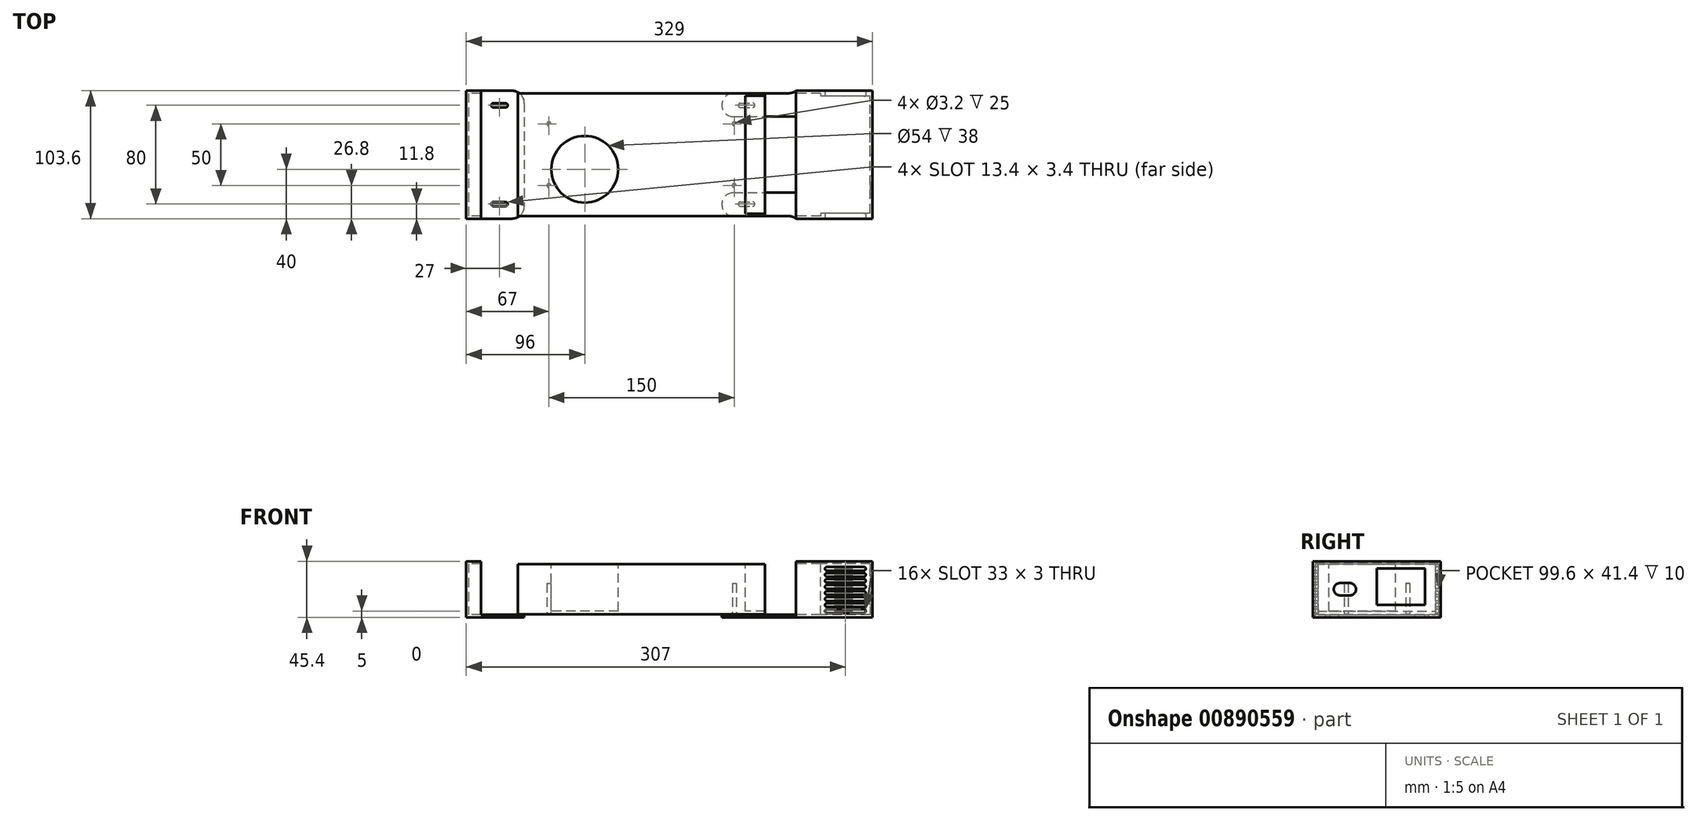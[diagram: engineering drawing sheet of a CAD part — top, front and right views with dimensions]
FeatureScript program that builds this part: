
annotation { "Feature Type Name" : "Feature", "Feature Type Description" : "" }
export const myFeature = defineFeature(function(context is Context, id is Id, definition is map)
    precondition{}
    {
        {
            var Q0;
            Q0=qCreatedBy(makeId("Top.planeOp"),FACE);
            var sketch = newSketch(context, id + "F0", { "sketchPlane" : qUnion([Q0])});
            skLineSegment(sketch, "E0.bottom", {"start": v(100, -49.8) * mm, "end": v(-100, -49.8) * mm});
            skLineSegment(sketch, "E0.top", {"start": v(100, 49.8) * mm, "end": v(-100, 49.8) * mm});
            skLineSegment(sketch, "E0.left", {"start": v(100, -49.8) * mm, "end": v(100, 49.8) * mm});
            skLineSegment(sketch, "E0.right", {"start": v(-100, -49.8) * mm, "end": v(-100, 49.8) * mm});
            skPoint(sketch, "E0.middle", {"position": v(0, 0) * mm});
            skSolve(sketch);
        }
        {
            var Q0;
            Q0=qSketchRegion(id+"F0",true);
            extrude(context, id + "F1", {"entities" : qUnion([Q0]), "depth" : 40.6 * mm, "offsetDistance" : 25 * mm});
        }
        {
            var Q0;
            Q0=makeQuery(id+"F1.opExtrude","CAP_FACE",FACE,{"disambiguationData":[OSD([sQuery(id+"F0.wireOp",EDGE,"E0.bottom"),sQuery(id+"F0.wireOp",EDGE,"E0.top"),sQuery(id+"F0.wireOp",EDGE,"E0.left"),sQuery(id+"F0.wireOp",EDGE,"E0.right")])],"isStart":false});
            var sketch = newSketch(context, id + "F2", { "sketchPlane" : qUnion([Q0])});
            skLineSegment(sketch, "E1.bottom", {"start": v(100, 47.8) * mm, "end": v(84, 47.8) * mm});
            skLineSegment(sketch, "E1.top", {"start": v(100, -47.8) * mm, "end": v(84, -47.8) * mm});
            skLineSegment(sketch, "E1.left", {"start": v(100, 47.8) * mm, "end": v(100, -47.8) * mm});
            skLineSegment(sketch, "E1.right", {"start": v(84, 47.8) * mm, "end": v(84, -47.8) * mm});
            skCircle(sketch, "E2", {"center": v(-46, -11.8) * mm, "radius": 27 * mm});
            skSolve(sketch);
        }
        {
            var Q0;
            Q0=qSketchRegion(id+"F2",true);
            extrude(context, id + "F3", {"entities" : qUnion([Q0]), "operationType" : NewBodyOperationType.REMOVE, "oppositeDirection" : true, "depth" : 38 * mm, "offsetDistance" : 25 * mm});
        }
        {
            var Q0;
            Q0=makeQuery(id+"F1.opExtrude","CAP_FACE",FACE,{"disambiguationData":[OSD([sQuery(id+"F0.wireOp",EDGE,"E0.bottom"),sQuery(id+"F0.wireOp",EDGE,"E0.top"),sQuery(id+"F0.wireOp",EDGE,"E0.left"),sQuery(id+"F0.wireOp",EDGE,"E0.right")])],"isStart":true});
            var sketch = newSketch(context, id + "F4", { "sketchPlane" : qUnion([Q0])});
            skCircle(sketch, "E3", {"center": v(-75, 25) * mm, "radius": 1.6 * mm});
            skCircle(sketch, "E4.MirrorC", {"center": v(75, 25) * mm, "radius": 1.6 * mm});
            skCircle(sketch, "E5.MirrorC", {"center": v(-75, -25) * mm, "radius": 1.6 * mm});
            skCircle(sketch, "E6.MirrorC", {"center": v(75, -25) * mm, "radius": 1.6 * mm});
            skSolve(sketch);
        }
        {
            var Q0;
            Q0=qSketchRegion(id+"F4",true);
            extrude(context, id + "F5", {"entities" : qUnion([Q0]), "operationType" : NewBodyOperationType.REMOVE, "oppositeDirection" : true, "depth" : 25 * mm, "offsetDistance" : 25 * mm});
        }
        {
            var Q0;
            Q0=makeQuery(id+"F1.opExtrude","SWEPT_FACE",FACE,{"disambiguationData":[OSD([sQuery(id+"F0.wireOp",EDGE,"E0.left")])]});
            cPlane(context, id + "F6", {"entities" : qUnion([Q0]), "cplaneType" : CPlaneType.OFFSET, "offset" : 25 * mm, "width" : 150 * mm, "height" : 150 * mm});
        }
        {
            var Q0;
            Q0=qCreatedBy(id+"F6.planeOp",FACE);
            var sketch = newSketch(context, id + "F7", { "sketchPlane" : qUnion([Q0])});
            skLineSegment(sketch, "E7.bottom", {"start": v(-47.4, 41) * mm, "end": v(47.4, 41) * mm});
            skLineSegment(sketch, "E7.top", {"start": v(-47.4, -0.4) * mm, "end": v(47.4, -0.4) * mm});
            skLineSegment(sketch, "E7.left", {"start": v(-47.4, 41) * mm, "end": v(-47.4, -0.4) * mm});
            skLineSegment(sketch, "E7.right", {"start": v(47.4, 41) * mm, "end": v(47.4, -0.4) * mm});
            skLineSegment(sketch, "E8.bottom", {"start": v(-51.8, 43) * mm, "end": v(51.8, 43) * mm});
            skLineSegment(sketch, "E8.top", {"start": v(-51.8, -2.4) * mm, "end": v(51.8, -2.4) * mm});
            skLineSegment(sketch, "E8.left", {"start": v(-51.8, 43) * mm, "end": v(-51.8, -2.4) * mm});
            skLineSegment(sketch, "E8.right", {"start": v(51.8, 43) * mm, "end": v(51.8, -2.4) * mm});
            skSolve(sketch);
        }
        {
            var Q0;
            Q0=qSketchRegion(id+"F7",true);
            extrude(context, id + "F8", {"entities" : qUnion([Q0]), "depth" : 60 * mm, "offsetDistance" : 25 * mm});
        }
        {
            var Q0;
            Q0=makeQuery(id+"F8.opExtrude","CAP_FACE",FACE,{"disambiguationData":[OSD([sQuery(id+"F7.wireOp",EDGE,"E7.bottom"),sQuery(id+"F7.wireOp",EDGE,"E7.top"),sQuery(id+"F7.wireOp",EDGE,"E7.left"),sQuery(id+"F7.wireOp",EDGE,"E7.right"),sQuery(id+"F7.wireOp",EDGE,"E8.bottom"),sQuery(id+"F7.wireOp",EDGE,"E8.top"),sQuery(id+"F7.wireOp",EDGE,"E8.left"),sQuery(id+"F7.wireOp",EDGE,"E8.right")])],"isStart":false});
            var sketch = newSketch(context, id + "F9", { "sketchPlane" : qUnion([Q0])});
            skSolve(sketch);
        }
        {
            var Q0;
            Q0=makeQuery(id+"F9.imprint","IMPRINT",FACE,{"disambiguationData":[TD([[makeQuery(id+"F9.imprint","IMPRINT",EDGE,{"derivedFrom":makeQuery(id+"F8.opExtrude","CAP_EDGE",EDGE,{"disambiguationData":[OSD([sQuery(id+"F7.wireOp",EDGE,"E7.bottom")])],"isStart":false})}),1.0]])]});
            var Q1;
            Q1=makeQuery(id+"F9.imprint","IMPRINT",FACE,{"disambiguationData":[TD([[makeQuery(id+"F9.imprint","IMPRINT",EDGE,{"derivedFrom":makeQuery(id+"F8.opExtrude","CAP_EDGE",EDGE,{"disambiguationData":[OSD([sQuery(id+"F7.wireOp",EDGE,"E7.bottom")])],"isStart":false})}),-1.0]])]});
            extrude(context, id + "F10", {"entities" : qUnion([Q0, Q1]), "operationType" : NewBodyOperationType.ADD, "depth" : 2 * mm, "offsetDistance" : 25 * mm});
        }
        {
            var Q0;
            Q0=makeQuery(id+"F10.opExtrude","CAP_FACE",FACE,{"disambiguationData":[OSD([sQuery(id+"F7.wireOp",EDGE,"E8.bottom"),sQuery(id+"F7.wireOp",EDGE,"E8.top"),sQuery(id+"F7.wireOp",EDGE,"E8.left"),sQuery(id+"F7.wireOp",EDGE,"E8.right")])],"isStart":false});
            var sketch = newSketch(context, id + "F11", { "sketchPlane" : qUnion([Q0])});
            skLineSegment(sketch, "E9.bottom", {"start": v(39, 7.7) * mm, "end": v(0, 7.7) * mm});
            skLineSegment(sketch, "E9.top", {"start": v(39, 37) * mm, "end": v(0, 37) * mm});
            skLineSegment(sketch, "E9.left", {"start": v(0, 37) * mm, "end": v(0, 7.7) * mm});
            skLineSegment(sketch, "E9.right", {"start": v(39, 37) * mm, "end": v(39, 7.7) * mm});
            skLineSegment(sketch, "E10", {"start": v(-29.9, 20.3) * mm, "end": v(-21.9, 20.3) * mm, "construction": true});
            skLineSegment(sketch, "E11", {"start": v(0, 43) * mm, "end": v(0, -2.4) * mm, "construction": true});
            skLineSegment(sketch, "E12", {"start": v(0, 43) * mm, "end": v(-51.8, 43) * mm, "construction": true});
            skPoint(sketch, "E13", {"position": v(-25.9, 20.3) * mm});
            skPoint(sketch, "E13.positionSnap0", {"position": v(0, 20.3) * mm});
            skPoint(sketch, "E13.positionSnap1", {"position": v(-25.9, 43) * mm});
            skArc(sketch, "E14.0.startCap", {"start": v(-29.9, 15.3) * mm, "mid": v(-34.9, 20.3) * mm, "end": v(-29.9, 25.3) * mm});
            skArc(sketch, "E14.0.endCap", {"start": v(-21.9, 25.3) * mm, "mid": v(-16.9, 20.3) * mm, "end": v(-21.9, 15.3) * mm});
            skLineSegment(sketch, "E14.0.left", {"start": v(-29.9, 25.3) * mm, "end": v(-21.9, 25.3) * mm});
            skLineSegment(sketch, "E14.0.right", {"start": v(-29.9, 15.3) * mm, "end": v(-21.9, 15.3) * mm});
            skSolve(sketch);
        }
        {
            var Q0;
            Q0=qSketchRegion(id+"F11",true);
            var Q1;
            Q1=makeQuery(id+"F10.opExtrude","CAP_FACE",FACE,{"disambiguationData":[OSD([sQuery(id+"F7.wireOp",EDGE,"E8.bottom"),sQuery(id+"F7.wireOp",EDGE,"E8.top"),sQuery(id+"F7.wireOp",EDGE,"E8.left"),sQuery(id+"F7.wireOp",EDGE,"E8.right")])],"isStart":true});
            extrude(context, id + "F12", {"entities" : qUnion([Q0]), "operationType" : NewBodyOperationType.REMOVE, "endBound" : BoundingType.UP_TO_SURFACE, "oppositeDirection" : true, "depth" : 25 * mm, "endBoundEntityFace" : qUnion([Q1]), "offsetDistance" : 25 * mm});
        }
        {
            var Q0;
            Q0=makeQuery(id+"F8.opExtrude","CAP_FACE",FACE,{"disambiguationData":[OSD([sQuery(id+"F7.wireOp",EDGE,"E7.bottom"),sQuery(id+"F7.wireOp",EDGE,"E7.top"),sQuery(id+"F7.wireOp",EDGE,"E7.left"),sQuery(id+"F7.wireOp",EDGE,"E7.right"),sQuery(id+"F7.wireOp",EDGE,"E8.bottom"),sQuery(id+"F7.wireOp",EDGE,"E8.top"),sQuery(id+"F7.wireOp",EDGE,"E8.left"),sQuery(id+"F7.wireOp",EDGE,"E8.right")])],"isStart":true});
            var sketch = newSketch(context, id + "F13", { "sketchPlane" : qUnion([Q0])});
            skPoint(sketch, "E15.oppositeSnap0", {"position": v(49.8, -4.1) * mm});
            skLineSegment(sketch, "E15.bottom", {"start": v(-49.8, -0.4) * mm, "end": v(49.8, -0.4) * mm});
            skLineSegment(sketch, "E15.top", {"start": v(-49.8, 41) * mm, "end": v(49.8, 41) * mm});
            skLineSegment(sketch, "E15.left", {"start": v(-49.8, -0.4) * mm, "end": v(-49.8, 41) * mm});
            skLineSegment(sketch, "E15.right", {"start": v(49.8, -0.4) * mm, "end": v(49.8, 41) * mm});
            skSolve(sketch);
        }
        {
            var Q0;
            Q0=qSketchRegion(id+"F13",true);
            extrude(context, id + "F14", {"entities" : qUnion([Q0]), "operationType" : NewBodyOperationType.REMOVE, "oppositeDirection" : true, "depth" : 20 * mm, "offsetDistance" : 25 * mm});
        }
        {
            var Q0;
            Q0=makeQuery(id+"F8.opExtrude","CAP_FACE",FACE,{"disambiguationData":[OSD([sQuery(id+"F7.wireOp",EDGE,"E7.bottom"),sQuery(id+"F7.wireOp",EDGE,"E7.top"),sQuery(id+"F7.wireOp",EDGE,"E7.left"),sQuery(id+"F7.wireOp",EDGE,"E7.right"),sQuery(id+"F7.wireOp",EDGE,"E8.bottom"),sQuery(id+"F7.wireOp",EDGE,"E8.top"),sQuery(id+"F7.wireOp",EDGE,"E8.left"),sQuery(id+"F7.wireOp",EDGE,"E8.right")])],"isStart":true});
            var sketch = newSketch(context, id + "F15", { "sketchPlane" : qUnion([Q0])});
            skLineSegment(sketch, "E16.bottom", {"start": v(-49.8, -2.4) * mm, "end": v(-30.8, -2.4) * mm});
            skLineSegment(sketch, "E16.top", {"start": v(-49.8, -0.4) * mm, "end": v(-30.8, -0.4) * mm});
            skLineSegment(sketch, "E16.left", {"start": v(-49.8, -2.4) * mm, "end": v(-49.8, -0.4) * mm});
            skLineSegment(sketch, "E16.right", {"start": v(-30.8, -2.4) * mm, "end": v(-30.8, -0.4) * mm});
            skLineSegment(sketch, "E17.bottom", {"start": v(49.8, -2.4) * mm, "end": v(30.8, -2.4) * mm});
            skLineSegment(sketch, "E17.top", {"start": v(49.8, -0.4) * mm, "end": v(30.8, -0.4) * mm});
            skLineSegment(sketch, "E17.left", {"start": v(49.8, -2.4) * mm, "end": v(49.8, -0.4) * mm});
            skLineSegment(sketch, "E17.right", {"start": v(30.8, -2.4) * mm, "end": v(30.8, -0.4) * mm});
            skSolve(sketch);
        }
        {
            var Q0;
            Q0=qSketchRegion(id+"F15",true);
            extrude(context, id + "F16", {"entities" : qUnion([Q0]), "operationType" : NewBodyOperationType.ADD, "depth" : 60 * mm, "offsetDistance" : 25 * mm});
        }
        {
            var Q0;
            Q0=makeQuery(id+"F16.opExtrude","CAP_EDGE",EDGE,{"disambiguationData":[OSD([sQuery(id+"F15.wireOp",EDGE,"E16.right")])],"isStart":false});
            var Q1;
            Q1=makeQuery(id+"F16.opExtrude","CAP_EDGE",EDGE,{"disambiguationData":[OSD([sQuery(id+"F15.wireOp",EDGE,"E16.left")])],"isStart":false});
            var Q2;
            Q2=makeQuery(id+"F16.opExtrude","CAP_EDGE",EDGE,{"disambiguationData":[OSD([sQuery(id+"F15.wireOp",EDGE,"E17.right")])],"isStart":false});
            var Q3;
            Q3=makeQuery(id+"F16.opExtrude","CAP_EDGE",EDGE,{"disambiguationData":[OSD([sQuery(id+"F15.wireOp",EDGE,"E17.left")])],"isStart":false});
            var Q4;
            Q4=makeQuery(id+"F16.opExtrude","CAP_EDGE",EDGE,{"disambiguationData":[OSD([sQuery(id+"F15.wireOp",EDGE,"E16.right")])],"isStart":true});
            var Q5;
            Q5=makeQuery(id+"F16.opExtrude","CAP_EDGE",EDGE,{"disambiguationData":[OSD([sQuery(id+"F15.wireOp",EDGE,"E17.right")])],"isStart":true});
            var Q6;
            Q6=makeQuery(id+"F16.opExtrude","CAP_EDGE",EDGE,{"disambiguationData":[OSD([sQuery(id+"F15.wireOp",EDGE,"E16.left")])],"isStart":true});
            var Q7;
            Q7=makeQuery(id+"F16.opExtrude","CAP_EDGE",EDGE,{"disambiguationData":[OSD([sQuery(id+"F15.wireOp",EDGE,"E17.left")])],"isStart":true});
            fillet(context, id + "F17", {"entities" : qUnion([Q0, Q1, Q2, Q3, Q4, Q5, Q6, Q7]), "radius" : 9.5 * mm, "tangentPropagation" : true, "allowEdgeOverflow" : false});
        }
        {
            var Q0;
            Q0=makeQuery(id+"F1.opExtrude","CAP_FACE",FACE,{"disambiguationData":[OSD([sQuery(id+"F0.wireOp",EDGE,"E0.bottom"),sQuery(id+"F0.wireOp",EDGE,"E0.top"),sQuery(id+"F0.wireOp",EDGE,"E0.left"),sQuery(id+"F0.wireOp",EDGE,"E0.right")])],"isStart":true});
            var sketch = newSketch(context, id + "F18", { "sketchPlane" : qUnion([Q0])});
            skLineSegment(sketch, "E18", {"start": v(80, 40) * mm, "end": v(90, 40) * mm, "construction": true});
            skLineSegment(sketch, "E19", {"start": v(100, 0) * mm, "end": v(192.1, 0) * mm, "construction": true});
            skArc(sketch, "E20.0.startCap", {"start": v(80, 38.3) * mm, "mid": v(78.3, 40) * mm, "end": v(80, 41.7) * mm});
            skArc(sketch, "E20.0.endCap", {"start": v(90, 41.7) * mm, "mid": v(91.7, 40) * mm, "end": v(90, 38.3) * mm});
            skLineSegment(sketch, "E20.0.left", {"start": v(80, 41.7) * mm, "end": v(90, 41.7) * mm});
            skLineSegment(sketch, "E20.0.right", {"start": v(80, 38.3) * mm, "end": v(90, 38.3) * mm});
            skLineSegment(sketch, "E21.MirrorCS", {"start": v(80, -38.3) * mm, "end": v(90, -38.3) * mm});
            skLineSegment(sketch, "E22.MirrorCS", {"start": v(80, -41.7) * mm, "end": v(90, -41.7) * mm});
            skArc(sketch, "E23.MirrorCS", {"start": v(80, -38.3) * mm, "mid": v(78.3, -40) * mm, "end": v(80, -41.7) * mm});
            skArc(sketch, "E24.MirrorCS", {"start": v(90, -41.7) * mm, "mid": v(91.7, -40) * mm, "end": v(90, -38.3) * mm});
            skLineSegment(sketch, "E25.MirrorCS", {"start": v(80, -40) * mm, "end": v(90, -40) * mm, "construction": true});
            skSolve(sketch);
        }
        {
            var Q0;
            Q0 = qSketchRegion(id + "F18", true);
            extrude(context, id + "F19", {"entities" : qUnion([Q0]), "operationType" : NewBodyOperationType.REMOVE, "endBound" : BoundingType.THROUGH_ALL, "depth" : 25 * mm, "offsetDistance" : 25 * mm});
        }
        {
            var Q0;
            {var subQ0=sQuery(id+"F7.wireOp",EDGE,"E8.left");Q0=makeQuery(id+"F10.boolean.opBoolean","MERGE",FACE,{"derivedFrom":[makeQuery(id+"F8.opExtrude","SWEPT_FACE",FACE,{"disambiguationData":[OSD([subQ0])]}),makeQuery(id+"F10.opExtrude","SWEPT_FACE",FACE,{"disambiguationData":[OSD([subQ0])]})]});}
            var sketch = newSketch(context, id + "F20", { "sketchPlane" : qUnion([Q0])});
            skLineSegment(sketch, "E26", {"start": v(150, 2.6) * mm, "end": v(180, 2.6) * mm, "construction": true});
            skArc(sketch, "E27.0.startCap", {"start": v(150, 1.1) * mm, "mid": v(148.5, 2.6) * mm, "end": v(150, 4.1) * mm});
            skArc(sketch, "E27.0.endCap", {"start": v(180, 4.1) * mm, "mid": v(181.5, 2.6) * mm, "end": v(180, 1.1) * mm});
            skLineSegment(sketch, "E27.0.left", {"start": v(150, 4.1) * mm, "end": v(180, 4.1) * mm});
            skLineSegment(sketch, "E27.0.right", {"start": v(150, 1.1) * mm, "end": v(180, 1.1) * mm});
            skLineSegment(sketch, "E28.0.1.0", {"start": v(150, 6) * mm, "end": v(180, 6) * mm});
            skArc(sketch, "E28.0.1.1", {"start": v(150, 6) * mm, "mid": v(148.5, 7.5) * mm, "end": v(150, 9) * mm});
            skArc(sketch, "E28.0.1.2", {"start": v(180, 9) * mm, "mid": v(181.5, 7.5) * mm, "end": v(180, 6) * mm});
            skLineSegment(sketch, "E28.0.1.3", {"start": v(150, 7.5) * mm, "end": v(180, 7.5) * mm, "construction": true});
            skLineSegment(sketch, "E28.0.1.4", {"start": v(150, 9) * mm, "end": v(180, 9) * mm});
            skLineSegment(sketch, "E28.0.2.0", {"start": v(150, 10.9) * mm, "end": v(180, 10.9) * mm});
            skArc(sketch, "E28.0.2.1", {"start": v(150, 10.9) * mm, "mid": v(148.5, 12.4) * mm, "end": v(150, 13.9) * mm});
            skArc(sketch, "E28.0.2.2", {"start": v(180, 13.9) * mm, "mid": v(181.5, 12.4) * mm, "end": v(180, 10.9) * mm});
            skLineSegment(sketch, "E28.0.2.3", {"start": v(150, 12.4) * mm, "end": v(180, 12.4) * mm, "construction": true});
            skLineSegment(sketch, "E28.0.2.4", {"start": v(150, 13.9) * mm, "end": v(180, 13.9) * mm});
            skLineSegment(sketch, "E28.0.3.0", {"start": v(150, 15.8) * mm, "end": v(180, 15.8) * mm});
            skArc(sketch, "E28.0.3.1", {"start": v(150, 15.8) * mm, "mid": v(148.5, 17.3) * mm, "end": v(150, 18.8) * mm});
            skArc(sketch, "E28.0.3.2", {"start": v(180, 18.8) * mm, "mid": v(181.5, 17.3) * mm, "end": v(180, 15.8) * mm});
            skLineSegment(sketch, "E28.0.3.3", {"start": v(150, 17.3) * mm, "end": v(180, 17.3) * mm, "construction": true});
            skLineSegment(sketch, "E28.0.3.4", {"start": v(150, 18.8) * mm, "end": v(180, 18.8) * mm});
            skLineSegment(sketch, "E28.0.4.0", {"start": v(150, 20.7) * mm, "end": v(180, 20.7) * mm});
            skArc(sketch, "E28.0.4.1", {"start": v(150, 20.7) * mm, "mid": v(148.5, 22.2) * mm, "end": v(150, 23.7) * mm});
            skArc(sketch, "E28.0.4.2", {"start": v(180, 23.7) * mm, "mid": v(181.5, 22.2) * mm, "end": v(180, 20.7) * mm});
            skLineSegment(sketch, "E28.0.4.3", {"start": v(150, 22.2) * mm, "end": v(180, 22.2) * mm, "construction": true});
            skLineSegment(sketch, "E28.0.4.4", {"start": v(150, 23.7) * mm, "end": v(180, 23.7) * mm});
            skLineSegment(sketch, "E28.0.5.0", {"start": v(150, 25.6) * mm, "end": v(180, 25.6) * mm});
            skArc(sketch, "E28.0.5.1", {"start": v(150, 25.6) * mm, "mid": v(148.5, 27.1) * mm, "end": v(150, 28.6) * mm});
            skArc(sketch, "E28.0.5.2", {"start": v(180, 28.6) * mm, "mid": v(181.5, 27.1) * mm, "end": v(180, 25.6) * mm});
            skLineSegment(sketch, "E28.0.5.3", {"start": v(150, 27.1) * mm, "end": v(180, 27.1) * mm, "construction": true});
            skLineSegment(sketch, "E28.0.5.4", {"start": v(150, 28.6) * mm, "end": v(180, 28.6) * mm});
            skLineSegment(sketch, "E28.0.6.0", {"start": v(150, 30.5) * mm, "end": v(180, 30.5) * mm});
            skArc(sketch, "E28.0.6.1", {"start": v(150, 30.5) * mm, "mid": v(148.5, 32) * mm, "end": v(150, 33.5) * mm});
            skArc(sketch, "E28.0.6.2", {"start": v(180, 33.5) * mm, "mid": v(181.5, 32) * mm, "end": v(180, 30.5) * mm});
            skLineSegment(sketch, "E28.0.6.3", {"start": v(150, 32) * mm, "end": v(180, 32) * mm, "construction": true});
            skLineSegment(sketch, "E28.0.6.4", {"start": v(150, 33.5) * mm, "end": v(180, 33.5) * mm});
            skLineSegment(sketch, "E28.0.7.0", {"start": v(150, 35.4) * mm, "end": v(180, 35.4) * mm});
            skArc(sketch, "E28.0.7.1", {"start": v(150, 35.4) * mm, "mid": v(148.5, 36.9) * mm, "end": v(150, 38.4) * mm});
            skArc(sketch, "E28.0.7.2", {"start": v(180, 38.4) * mm, "mid": v(181.5, 36.9) * mm, "end": v(180, 35.4) * mm});
            skLineSegment(sketch, "E28.0.7.3", {"start": v(150, 36.9) * mm, "end": v(180, 36.9) * mm, "construction": true});
            skLineSegment(sketch, "E28.0.7.4", {"start": v(150, 38.4) * mm, "end": v(180, 38.4) * mm});
            skLineSegment(sketch, "E28.direction1", {"start": v(150, 1.1) * mm, "end": v(175, 1.1) * mm, "construction": true});
            skLineSegment(sketch, "E28.direction2", {"start": v(150, 1.1) * mm, "end": v(150, 6) * mm, "construction": true});
            skSolve(sketch);
        }
        {
            var Q0;
            Q0 = qSketchRegion(id + "F20", true);
            extrude(context, id + "F21", {"entities" : qUnion([Q0]), "operationType" : NewBodyOperationType.REMOVE, "endBound" : BoundingType.THROUGH_ALL, "oppositeDirection" : true, "depth" : 25 * mm, "offsetDistance" : 25 * mm});
        }
        {
            var Q0;
            Q0=makeQuery(id+"F1.opExtrude","SWEPT_FACE",FACE,{"disambiguationData":[OSD([sQuery(id+"F0.wireOp",EDGE,"E0.right")])]});
            cPlane(context, id + "F22", {"entities" : qUnion([Q0]), "cplaneType" : CPlaneType.OFFSET, "offset" : 40 * mm, "width" : 150 * mm, "height" : 150 * mm});
        }
        {
            var Q0;
            Q0=qCreatedBy(id+"F22.planeOp",FACE);
            var sketch = newSketch(context, id + "F23", { "sketchPlane" : qUnion([Q0])});
            skLineSegment(sketch, "E29.bottom", {"start": v(-51.8, 43) * mm, "end": v(51.8, 43) * mm});
            skLineSegment(sketch, "E29.top", {"start": v(-51.8, -2.4) * mm, "end": v(51.8, -2.4) * mm});
            skLineSegment(sketch, "E29.left", {"start": v(-51.8, 43) * mm, "end": v(-51.8, -2.4) * mm});
            skLineSegment(sketch, "E29.right", {"start": v(51.8, 43) * mm, "end": v(51.8, -2.4) * mm});
            skLineSegment(sketch, "E30.bottom", {"start": v(-49.8, 41) * mm, "end": v(49.8, 41) * mm});
            skLineSegment(sketch, "E30.top", {"start": v(-49.8, -0.4) * mm, "end": v(49.8, -0.4) * mm});
            skLineSegment(sketch, "E30.left", {"start": v(-49.8, 41) * mm, "end": v(-49.8, -0.4) * mm});
            skLineSegment(sketch, "E30.right", {"start": v(49.8, 41) * mm, "end": v(49.8, -0.4) * mm});
            skSolve(sketch);
        }
        {
            var Q0;
            Q0 = qSketchRegion(id + "F23", true);
            extrude(context, id + "F24", {"entities" : qUnion([Q0]), "oppositeDirection" : true, "depth" : 10 * mm, "offsetDistance" : 25 * mm});
        }
        {
            var Q0;
            Q0=makeQuery(id+"F24.opExtrude","CAP_FACE",FACE,{"disambiguationData":[OSD([sQuery(id+"F23.wireOp",EDGE,"E29.bottom"),sQuery(id+"F23.wireOp",EDGE,"E29.top"),sQuery(id+"F23.wireOp",EDGE,"E29.left"),sQuery(id+"F23.wireOp",EDGE,"E29.right"),sQuery(id+"F23.wireOp",EDGE,"E30.bottom"),sQuery(id+"F23.wireOp",EDGE,"E30.top"),sQuery(id+"F23.wireOp",EDGE,"E30.left"),sQuery(id+"F23.wireOp",EDGE,"E30.right")])],"isStart":true});
            var sketch = newSketch(context, id + "F25", { "sketchPlane" : qUnion([Q0])});
            skLineSegment(sketch, "E31.bottom", {"start": v(-51.8, 43) * mm, "end": v(51.8, 43) * mm});
            skLineSegment(sketch, "E31.top", {"start": v(-51.8, -2.4) * mm, "end": v(51.8, -2.4) * mm});
            skLineSegment(sketch, "E31.left", {"start": v(-51.8, 43) * mm, "end": v(-51.8, -2.4) * mm});
            skLineSegment(sketch, "E31.right", {"start": v(51.8, 43) * mm, "end": v(51.8, -2.4) * mm});
            skSolve(sketch);
        }
        {
            var Q0;
            Q0 = qSketchRegion(id + "F25", true);
            extrude(context, id + "F26", {"entities" : qUnion([Q0]), "operationType" : NewBodyOperationType.ADD, "depth" : 2 * mm, "offsetDistance" : 25 * mm});
        }
        {
            var Q0;
            Q0=makeQuery(id+"F24.opExtrude","CAP_FACE",FACE,{"disambiguationData":[OSD([sQuery(id+"F23.wireOp",EDGE,"E29.bottom"),sQuery(id+"F23.wireOp",EDGE,"E29.top"),sQuery(id+"F23.wireOp",EDGE,"E29.left"),sQuery(id+"F23.wireOp",EDGE,"E29.right"),sQuery(id+"F23.wireOp",EDGE,"E30.bottom"),sQuery(id+"F23.wireOp",EDGE,"E30.top"),sQuery(id+"F23.wireOp",EDGE,"E30.left"),sQuery(id+"F23.wireOp",EDGE,"E30.right")])],"isStart":false});
            var sketch = newSketch(context, id + "F27", { "sketchPlane" : qUnion([Q0])});
            skLineSegment(sketch, "E32.bottom", {"start": v(-51.8, -2.4) * mm, "end": v(51.8, -2.4) * mm});
            skLineSegment(sketch, "E32.top", {"start": v(-51.8, -0.4) * mm, "end": v(51.8, -0.4) * mm});
            skLineSegment(sketch, "E32.left", {"start": v(-51.8, -2.4) * mm, "end": v(-51.8, -0.4) * mm});
            skLineSegment(sketch, "E32.right", {"start": v(51.8, -2.4) * mm, "end": v(51.8, -0.4) * mm});
            skSolve(sketch);
        }
        {
            var Q0;
            Q0 = qSketchRegion(id + "F27", true);
            extrude(context, id + "F28", {"entities" : qUnion([Q0]), "operationType" : NewBodyOperationType.ADD, "depth" : 35 * mm, "offsetDistance" : 25 * mm});
        }
        {
            var Q0;
            Q0=makeQuery(id+"F28.opExtrude","CAP_EDGE",EDGE,{"disambiguationData":[OSD([sQuery(id+"F27.wireOp",EDGE,"E32.left")])],"isStart":false});
            var Q1;
            Q1=makeQuery(id+"F28.opExtrude","CAP_EDGE",EDGE,{"disambiguationData":[OSD([sQuery(id+"F27.wireOp",EDGE,"E32.right")])],"isStart":false});
            fillet(context, id + "F29", {"entities" : qUnion([Q0, Q1]), "radius" : 10 * mm, "tangentPropagation" : true, "allowEdgeOverflow" : false});
        }
        {
            var Q0;
            Q0=makeQuery(id+"F28.boolean.opBoolean","MERGE",FACE,{"derivedFrom":[makeQuery(id+"F26.boolean.opBoolean","MERGE",FACE,{"derivedFrom":[makeQuery(id+"F24.opExtrude","SWEPT_FACE",FACE,{"disambiguationData":[OSD([sQuery(id+"F23.wireOp",EDGE,"E29.top")])]}),makeQuery(id+"F26.opExtrude","SWEPT_FACE",FACE,{"disambiguationData":[OSD([sQuery(id+"F25.wireOp",EDGE,"E31.top")])]})]}),makeQuery(id+"F28.opExtrude","SWEPT_FACE",FACE,{"disambiguationData":[OSD([sQuery(id+"F27.wireOp",EDGE,"E32.bottom")])]})]});
            var sketch = newSketch(context, id + "F30", { "sketchPlane" : qUnion([Q0])});
            skLineSegment(sketch, "E33", {"start": v(78.3, 40) * mm, "end": v(-114.6, 40) * mm, "construction": true});
            skLineSegment(sketch, "E34", {"start": v(-120, 40) * mm, "end": v(-110, 40) * mm, "construction": true});
            skArc(sketch, "E35.0.startCap", {"start": v(-120, 38.3) * mm, "mid": v(-121.7, 40) * mm, "end": v(-120, 41.7) * mm});
            skArc(sketch, "E35.0.endCap", {"start": v(-110, 41.7) * mm, "mid": v(-108.3, 40) * mm, "end": v(-110, 38.3) * mm});
            skLineSegment(sketch, "E35.0.left", {"start": v(-120, 41.7) * mm, "end": v(-110, 41.7) * mm});
            skLineSegment(sketch, "E35.0.right", {"start": v(-120, 38.3) * mm, "end": v(-110, 38.3) * mm});
            skLineSegment(sketch, "E36", {"start": v(-95, 0) * mm, "end": v(-142, 0) * mm, "construction": true});
            skArc(sketch, "E37.MirrorCS", {"start": v(-120, -38.3) * mm, "mid": v(-121.7, -40) * mm, "end": v(-120, -41.7) * mm});
            skLineSegment(sketch, "E38.MirrorCS", {"start": v(-120, -41.7) * mm, "end": v(-110, -41.7) * mm});
            skArc(sketch, "E39.MirrorCS", {"start": v(-110, -41.7) * mm, "mid": v(-108.3, -40) * mm, "end": v(-110, -38.3) * mm});
            skLineSegment(sketch, "E40.MirrorCS", {"start": v(-120, -40) * mm, "end": v(-110, -40) * mm, "construction": true});
            skLineSegment(sketch, "E41.MirrorCS", {"start": v(-120, -38.3) * mm, "end": v(-110, -38.3) * mm});
            skSolve(sketch);
        }
        {
            var Q0;
            Q0 = qSketchRegion(id + "F30", true);
            var Q1;
            Q1=makeQuery(id+"F28.boolean.opBoolean","MERGE",FACE,{"derivedFrom":[makeQuery(id+"F24.opExtrude","SWEPT_FACE",FACE,{"disambiguationData":[OSD([sQuery(id+"F23.wireOp",EDGE,"E30.top")])]}),makeQuery(id+"F28.opExtrude","SWEPT_FACE",FACE,{"disambiguationData":[OSD([sQuery(id+"F27.wireOp",EDGE,"E32.top")])]})]});
            extrude(context, id + "F31", {"entities" : qUnion([Q0]), "operationType" : NewBodyOperationType.REMOVE, "endBound" : BoundingType.UP_TO_SURFACE, "oppositeDirection" : true, "depth" : 25 * mm, "endBoundEntityFace" : qUnion([Q1]), "offsetDistance" : 25 * mm});
        }
    });
